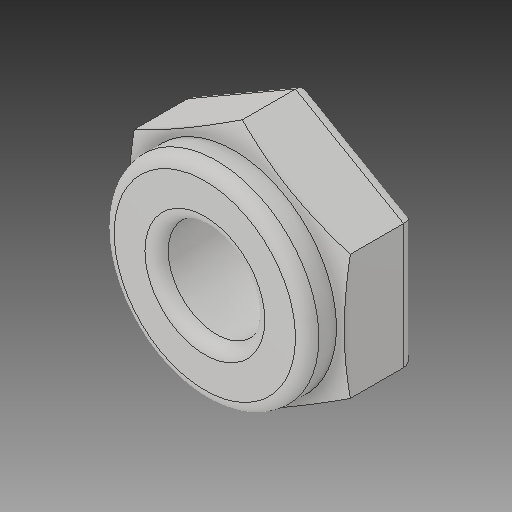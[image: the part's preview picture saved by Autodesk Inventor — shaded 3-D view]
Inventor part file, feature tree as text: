
AUTODESK INVENTOR PART (.ipt)
format: ipt  version: 2017 (Build 210142000, 142)  size: 157,696 bytes
history: native  units: in
note: dims shown in document units (in); Inventor stores cm internally (conversion verified against a paired STEP export)
features: fillet x1
ambient origin geometry x8: Origin, YZ Plane, XZ Plane, XY Plane, X Axis, Y Axis, Z Axis, Center Point
bodies: Solid1 (feature_tree)
feature tree (1):
  fillet  "Fillet4"  [1 undecoded]
note: 1 required parameter value undecoded (feature->parameter linkage not recoverable at this tier; creation-order binding heuristic only, values carry confidence <= 0.55)
